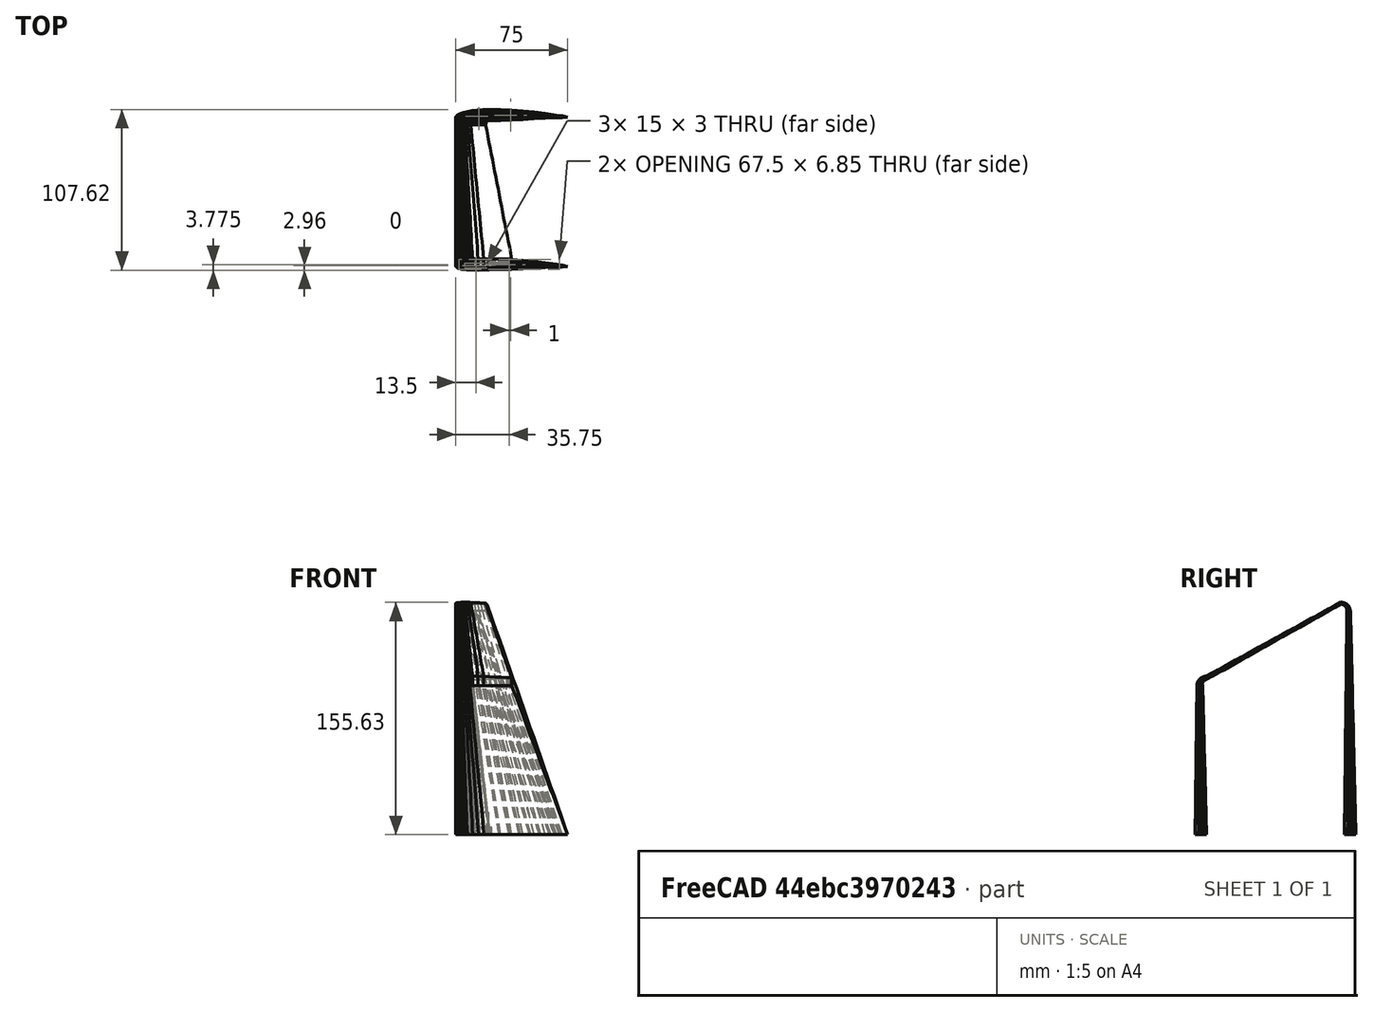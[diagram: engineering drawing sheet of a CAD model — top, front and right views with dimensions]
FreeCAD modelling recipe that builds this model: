
FCSTD DOCUMENT  (FreeCAD 0.16R6712 (Git))
Label: Aile_double_babord_2
License: All rights reserved
LicenseURL: http://en.wikipedia.org/wiki/All_rights_reserved
objects: Part::FeaturePython×6, Part::Loft×5, Part::Part2DObjectPython×4, Sketcher::SketchObject×3, Part::Cut×2, Part::Sweep×2, PartDesign::Pad×2, Mesh::Feature×2, Part::MultiFuse×1
note: 27 computed .brp shape members not serialized (recipe doc carries the construction recipe); baked Part::Feature solids carry a one-line shape summary decoded from their .brp

FEATURE [Part::Part2DObjectPython] DWire  label="DWire_base"  # Draft 2D object (typed FeaturePython)
  ChamferSize = 0
  Closed = true
  End = (75,-0.07875,0)
  FilletRadius = 0
  Length = 152.352
  MakeFace = true
  Points = (35) [(75,0.07875,0),(71.2807,0.7425,0),(67.5502,1.362,0),(60.0727,2.472,0),(52.5765,3.41325,0),(45.0637,4.185,0),(37.5367,4.767,0),(30,5.12775,0),+27 more]
  Start = (75,0.07875,0)
  Subdivisions = 0
FEATURE [Part::FeaturePython] Scale  label="Scale_bout"  # Draft clone (typed FeaturePython)
  Objects = -> [DWire]
  Placement = pos=(0,0,100) rot=(0,0,1;0rad)
  Scale = (0.5,0.5,1)
FEATURE [Part::FeaturePython] Scale001  label="Scale_int_base"  # Draft clone (typed FeaturePython)
  Objects = -> [DWire]
  Placement = pos=(2,0.1,0) rot=(0,0,1;0rad)
  Scale = (0.9,0.9,0.9)
FEATURE [Part::FeaturePython] Scale002  label="Scale_int_bout"  # Draft clone (typed FeaturePython)
  Objects = -> [Scale]
  Placement = pos=(3,0.2,100) rot=(0,0,1;0rad)
  Scale = (0.7,0.7,1)
FEATURE [Part::Loft] Loft
  Closed = false
  Ruled = false
  Sections = -> [DWire,Scale]
  Solid = true
FEATURE [Part::Loft] Loft001
  Closed = false
  Ruled = false
  Sections = -> [Scale001,Scale002]
  Solid = true
FEATURE [Part::Cut] Cut
  Base = -> Loft
  Tool = -> Loft001
FEATURE [Part::Part2DObjectPython] DWire001  label="DWire_base_haut"  # Draft 2D object (typed FeaturePython)
  ChamferSize = 0
  Closed = true
  End = (75,99.9213,0)
  FilletRadius = 0
  Length = 152.352
  MakeFace = true
  Placement = pos=(0,100,0) rot=(0,0,1;0rad)
  Points = (35) [(75,0.07875,0),(71.2807,0.7425,0),(67.5502,1.362,0),(60.0727,2.472,0),(52.5765,3.41325,0),(45.0637,4.185,0),(37.5367,4.767,0),(30,5.12775,0),+27 more]
  Start = (75,100.079,0)
  Subdivisions = 0
FEATURE [Part::FeaturePython] Scale003  label="Scale_int_base_haut"  # Draft clone (typed FeaturePython)
  Objects = -> [DWire001]
  Placement = pos=(3,110.1,0) rot=(0,0,1;0rad)
  Scale = (0.9,0.9,1)
FEATURE [Part::FeaturePython] Scale004  label="Scale_bout_haut"  # Draft clone (typed FeaturePython)
  Objects = -> [DWire001]
  Placement = pos=(0,170,150) rot=(0,0,1;0rad)
  Scale = (0.3,0.3,1)
FEATURE [Part::FeaturePython] Scale005  label="Scale_int_bout_haut"  # Draft clone (typed FeaturePython)
  Objects = -> [Scale004]
  Placement = pos=(3,220.2,150) rot=(0,0,1;0rad)
  Scale = (0.5,0.5,1)
FEATURE [Part::Loft] Loft002
  Closed = false
  Ruled = false
  Sections = -> [DWire001,Scale004]
  Solid = true
FEATURE [Part::Loft] Loft003
  Closed = false
  Ruled = false
  Sections = -> [Scale003,Scale005]
  Solid = true
FEATURE [Part::Cut] Cut001
  Base = -> Loft002
  Tool = -> Loft003
FEATURE [Part::Part2DObjectPython] DWire002  # Draft 2D object (typed FeaturePython)
  ChamferSize = 0
  Closed = true
  End = (37.5,5,104.976)
  FilletRadius = 0
  Length = 75.448
  MakeFace = true
  Placement = pos=(0,5,105) rot=(1,0,0;1.5708rad)
  Points = (35) [(37.5,0.023625,0),(35.625,0.151125,0),(33.75,0.2715,0),(30,0.492,0),(26.25,0.687,0),(22.5,0.85575,0),(18.75,0.992625,0),(15,1.08825,0),+27 more]
  Start = (37.5,5,105.024)
  Subdivisions = 0
FEATURE [Sketcher::SketchObject] Sketch
  Placement = pos=(0,0,0) rot=(0.57735,0.57735,0.57735;2.0944rad)
  sketch-geometry (5):
    g0: ArcOfCircle CenterX=95 CenterY=150 CenterZ=0 NormalX=0 NormalY=0 NormalZ=1 Radius=4.99999 StartAngle=6.28318 EndAngle=7.85398
    g1: ArcOfCircle CenterX=5.00002 CenterY=100 CenterZ=0 NormalX=0 NormalY=0 NormalZ=1 Radius=5.00002 StartAngle=1.5708 EndAngle=3.14159
    g2: LineSegment [constr] StartX=5 StartY=105 StartZ=0 EndX=0 EndY=102.113 EndZ=0
    g3: LineSegment [constr] StartX=100 StartY=150 StartZ=0 EndX=100 EndY=144.155 EndZ=0
    g4: LineSegment [constr] StartX=95 StartY=155 StartZ=0 EndX=101.436 EndY=158.716 EndZ=0
  constraints (17):
    c: PointOnObject(g1,g-2)
    c: DistanceY(g-1,g1) = 100
    c: DistanceX(g1,g1) = 5
    c: DistanceY(g1,g1) = 5
    c: PointOnObject(g2,g-2)
    c: Angle(g-2,g2) = 2.0944
    c: Coincident(g2,g1)
    c: Tangent(g1,g-2)
    c: DistanceX(g-1,g0) = 95
    c: DistanceX(g-1,g0) = 100
    c: DistanceY(g-1,g0) = 150
    c: DistanceY(g0,g0) = 5
    c: Vertical(g3)
    c: Coincident(g4,g0)
    c: Angle(g4,g3) = 1.0472
    c: Tangent(g0,g3)
    c: Coincident(g3,g0)
FEATURE [Part::Part2DObjectPython] DWire004  # Draft 2D object (typed FeaturePython)
  ChamferSize = 0
  Closed = true
  End = (20,95,154.987)
  FilletRadius = 0
  Length = 40.2389
  MakeFace = true
  Placement = pos=(0,95,155) rot=(1,0,0;1.5708rad)
  Points = (35) [(20,0.0126,0),(19,0.0806,0),(18,0.1448,0),(16,0.2624,0),(14,0.3664,0),(12,0.4564,0),(10,0.5294,0),(8,0.5804,0),(6,0.6002,0),(5,0.5942,0),(4,0.5738,0),+24 more]
  Start = (20,95,155.013)
  Subdivisions = 0
FEATURE [Part::Loft] Loft005
  Closed = false
  Ruled = false
  Sections = -> [DWire002,DWire004]
  Solid = true
FEATURE [Part::Sweep] Sweep
  Frenet = false
  Sections = -> [DWire004,Scale004]
  Solid = true
  Spine = -> Sketch [Edge1]
  Transition = 1
FEATURE [Part::Sweep] Sweep001
  Frenet = false
  Sections = -> [DWire002,Scale]
  Solid = true
  Spine = -> Sketch [Edge2]
  Transition = 1
FEATURE [Part::MultiFuse] Fusion
  Shapes = -> [Sweep001,Loft005,Sweep,Cut001,Cut]
FEATURE [Sketcher::SketchObject] Sketch001
  ExternalGeometry = -> [Fusion]
  Placement = pos=(0,0,0) rot=(1,0,0;3.14159rad)
  Support = -> Fusion [Face16]
  sketch-geometry (20):
    g0: LineSegment StartX=6 StartY=1 StartZ=0 EndX=21 EndY=1 EndZ=0
    g1: LineSegment StartX=21 StartY=1 StartZ=0 EndX=21 EndY=-2 EndZ=0
    g2: LineSegment StartX=21 StartY=-2 StartZ=0 EndX=6 EndY=-2 EndZ=0
    g3: LineSegment StartX=6 StartY=-2 StartZ=0 EndX=6 EndY=1 EndZ=0
    g4: LineSegment StartX=5 StartY=1.45606 StartZ=0 EndX=5 EndY=-2.32561 EndZ=0
    g5: LineSegment StartX=22 StartY=2.01648 StartZ=0 EndX=22 EndY=-4.73385 EndZ=0
    g6: LineSegment StartX=5 StartY=1.45606 StartZ=0 EndX=5.54915 EndY=1.57535 EndZ=0
    g7: LineSegment StartX=5.54915 StartY=1.57535 StartZ=0 EndX=7.25352 EndY=1.79608 EndZ=0
    g8: LineSegment StartX=7.25352 StartY=1.79608 StartZ=0 EndX=8.94575 EndY=1.9358 EndZ=0
    g9: LineSegment StartX=8.94575 StartY=1.9358 StartZ=0 EndX=12.3126 EndY=2.07823 EndZ=0
    g10: LineSegment StartX=12.3126 StartY=2.07823 StartZ=0 EndX=15.6613 EndY=2.1113 EndZ=0
    g11: LineSegment StartX=15.6613 StartY=2.1113 StartZ=0 EndX=19.0006 EndY=2.08025 EndZ=0
    g12: LineSegment StartX=19.0006 StartY=2.08025 StartZ=0 EndX=22 EndY=2.01648 EndZ=0
    g13: LineSegment StartX=22 StartY=-4.73385 StartZ=0 EndX=18.7494 EndY=-4.6009 EndZ=0
    g14: LineSegment StartX=18.7494 StartY=-4.6009 StartZ=0 EndX=15.3387 EndY=-4.3363 EndZ=0
    g15: LineSegment StartX=15.3387 StartY=-4.3363 StartZ=0 EndX=11.9374 EndY=-3.92387 EndZ=0
    g16: LineSegment StartX=11.9374 StartY=-3.92387 StartZ=0 EndX=8.55425 EndY=-3.31705 EndZ=0
    g17: LineSegment StartX=8.55425 StartY=-3.31705 StartZ=0 EndX=6.87148 EndY=-2.91407 EndZ=0
    g18: LineSegment StartX=6.87148 StartY=-2.91407 StartZ=0 EndX=5.20085 EndY=-2.4085 EndZ=0
    g19: LineSegment StartX=5.20085 StartY=-2.4085 StartZ=0 EndX=5 EndY=-2.32561 EndZ=0
  constraints (47):
    c: Coincident(g0,g1)
    c: Coincident(g1,g2)
    c: Coincident(g2,g3)
    c: Coincident(g3,g0)
    c: Horizontal(g0)
    c: Horizontal(g2)
    c: Vertical(g1)
    c: Vertical(g3)
    c: DistanceY(g1,g1) = 3
    c: DistanceX(g0,g0) = 15
    c: Vertical(g4)
    c: Vertical(g5)
    c: DistanceX(g4,g0) = 1
    c: DistanceX(g0,g5) = 1
    c: DistanceX(g-1,g0) = 6
    c: PointOnObject(g4,g-4)
    c: PointOnObject(g4,g-3)
    c: PointOnObject(g5,g-11)
    c: PointOnObject(g5,g-10)
    c: Coincident(g6,g4)
    c: Coincident(g6,g-16)
    c: Coincident(g7,g6)
    c: Coincident(g7,g-16)
    c: Coincident(g8,g7)
    c: Coincident(g8,g-15)
    c: Coincident(g9,g8)
    c: Coincident(g9,g-14)
    c: Coincident(g10,g9)
    c: Coincident(g10,g-13)
    c: Coincident(g11,g10)
    c: Coincident(g11,g-12)
    c: Coincident(g12,g11)
    c: Coincident(g12,g5)
    c: Coincident(g13,g5)
    c: Coincident(g13,g-10)
    c: Coincident(g14,g13)
    c: Coincident(g14,g-9)
    c: Coincident(g15,g14)
    c: Coincident(g15,g-8)
    c: Coincident(g16,g15)
    c: Coincident(g16,g-7)
    c: Coincident(g17,g16)
    c: Coincident(g18,g17)
    c: Coincident(g18,g-5)
    c: Coincident(g19,g18)
    c: Coincident(g19,g4)
    c: DistanceY(g-1,g0) = 1
FEATURE [PartDesign::Pad] Pad
  Length = 15
  Length2 = 100
  Reversed = true
  Sketch = -> Sketch001
  Type = 0
FEATURE [Sketcher::SketchObject] Sketch002
  ExternalGeometry = -> [Pad]
  Placement = pos=(0,0,0) rot=(1,0,0;3.14159rad)
  Support = -> Pad [Face223]
  sketch-geometry (18):
    g0: LineSegment StartX=8 StartY=-99 StartZ=0 EndX=23 EndY=-99 EndZ=0
    g1: LineSegment StartX=23 StartY=-99 StartZ=0 EndX=23 EndY=-102 EndZ=0
    g2: LineSegment StartX=23 StartY=-102 StartZ=0 EndX=8 EndY=-102 EndZ=0
    g3: LineSegment StartX=8 StartY=-102 StartZ=0 EndX=8 EndY=-99 EndZ=0
    g4: LineSegment StartX=7 StartY=-97.7972 StartZ=0 EndX=7 EndY=-103.507 EndZ=0
    g5: LineSegment StartX=24 StartY=-97.6973 StartZ=0 EndX=24 EndY=-105.15 EndZ=0
    g6: LineSegment StartX=7 StartY=-103.507 StartZ=0 EndX=7.2825 EndY=-103.575 EndZ=0
    g7: LineSegment StartX=7.2825 StartY=-103.575 StartZ=0 EndX=11.0415 EndY=-104.249 EndZ=0
    g8: LineSegment StartX=11.0415 StartY=-104.249 StartZ=0 EndX=14.8208 EndY=-104.707 EndZ=0
    g9: LineSegment StartX=14.8208 StartY=-104.707 StartZ=0 EndX=18.6105 EndY=-105.001 EndZ=0
    g10: LineSegment StartX=18.6105 StartY=-105.001 StartZ=0 EndX=22.4062 EndY=-105.156 EndZ=0
    g11: LineSegment StartX=22.4062 StartY=-105.156 StartZ=0 EndX=24 EndY=-105.15 EndZ=0
    g12: LineSegment StartX=24 StartY=-97.6973 StartZ=0 EndX=22.5938 EndY=-97.6562 EndZ=0
    g13: LineSegment StartX=22.5938 StartY=-97.6562 StartZ=0 EndX=18.8895 EndY=-97.5775 EndZ=0
    g14: LineSegment StartX=18.8895 StartY=-97.5775 StartZ=0 EndX=15.1792 EndY=-97.543 EndZ=0
    g15: LineSegment StartX=15.1792 StartY=-97.543 StartZ=0 EndX=11.4585 EndY=-97.5798 EndZ=0
    g16: LineSegment StartX=11.4585 StartY=-97.5798 StartZ=0 EndX=7.7175 EndY=-97.738 EndZ=0
    g17: LineSegment StartX=7.7175 StartY=-97.738 StartZ=0 EndX=7 EndY=-97.7972 EndZ=0
  constraints (46):
    c: Coincident(g0,g1)
    c: Coincident(g1,g2)
    c: Coincident(g2,g3)
    c: Coincident(g3,g0)
    c: Horizontal(g0)
    c: Horizontal(g2)
    c: Vertical(g1)
    c: Vertical(g3)
    c: DistanceY(g1,g1) = 3
    c: DistanceX(g2,g2) = 15
    c: DistanceX(g-3,g0) = 8
    c: DistanceY(g-3,g0) = 1
    c: Vertical(g4)
    c: Vertical(g5)
    c: DistanceX(g0,g5) = 1
    c: DistanceX(g4,g0) = 1
    c: PointOnObject(g4,g-15)
    c: PointOnObject(g4,g-4)
    c: PointOnObject(g5,g-9)
    c: PointOnObject(g5,g-10)
    c: Coincident(g6,g4)
    c: Coincident(g6,g-15)
    c: Coincident(g7,g6)
    c: Coincident(g7,g-14)
    c: PointOnObject(g8,g-13)
    c: Coincident(g8,g-13)
    c: Coincident(g7,g8)
    c: Coincident(g7,g-13)
    c: Coincident(g9,g8)
    c: Coincident(g9,g-12)
    c: Coincident(g10,g-11)
    c: Coincident(g11,g10)
    c: Coincident(g11,g5)
    c: Coincident(g9,g10)
    c: Coincident(g12,g5)
    c: Coincident(g12,g-9)
    c: Coincident(g13,g12)
    c: Coincident(g13,g-8)
    c: Coincident(g14,g13)
    c: Coincident(g14,g-7)
    c: Coincident(g15,g14)
    c: Coincident(g15,g-6)
    c: Coincident(g16,g15)
    c: Coincident(g16,g-5)
    c: Coincident(g17,g16)
    c: Coincident(g17,g4)
FEATURE [PartDesign::Pad] Pad001
  Length = 5
  Length2 = 100
  Reversed = true
  Sketch = -> Sketch002
  Type = 0
FEATURE [Mesh::Feature] Aile_renfort_interne
  Placement = pos=(6,-1,-15) rot=(0,0,1;0rad)
FEATURE [Mesh::Feature] Aile_renfort_interne001
  Placement = pos=(8,99,-25) rot=(0,0,1;0rad)
